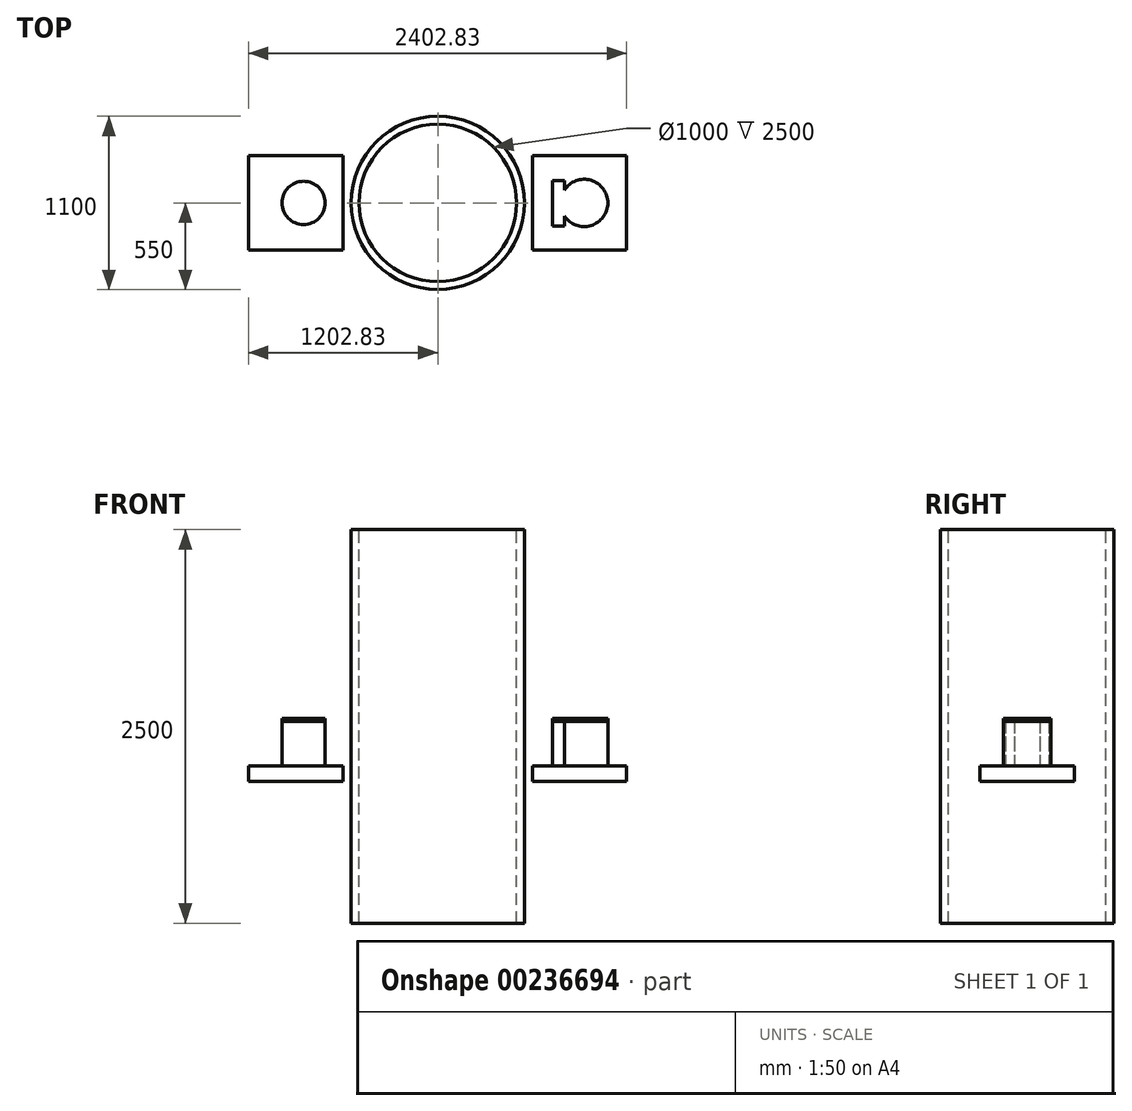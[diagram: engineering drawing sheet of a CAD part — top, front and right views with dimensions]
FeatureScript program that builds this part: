
annotation { "Feature Type Name" : "Feature", "Feature Type Description" : "" }
export const myFeature = defineFeature(function(context is Context, id is Id, definition is map)
    precondition{}
    {
        {
            var Q0;
            Q0=qCreatedBy(makeId("Top.planeOp"),FACE);
            var sketch = newSketch(context, id + "F0", { "sketchPlane" : qUnion([Q0])});
            skCircle(sketch, "E0", {"center": v(0, 0) * mm, "radius": 500 * mm});
            skCircle(sketch, "E1", {"center": v(0, 0) * mm, "radius": 550 * mm});
            skSolve(sketch);
        }
        {
            var Q0;
            Q0 = qSketchRegion(id + "F0", true);
            extrude(context, id + "F1", {"entities" : qUnion([Q0]), "oppositeDirection" : true, "depth" : 2500 * mm, "offsetDistance" : 25 * mm});
        }
        {
            var Q0;
            Q0=qCreatedBy(makeId("Front.planeOp"),FACE);
            var sketch = newSketch(context, id + "F2", { "sketchPlane" : qUnion([Q0])});
            skLineSegment(sketch, "E2.bottom", {"start": v(600, -1500) * mm, "end": v(1200, -1500) * mm});
            skLineSegment(sketch, "E2.top", {"start": v(600, -1600) * mm, "end": v(1200, -1600) * mm});
            skLineSegment(sketch, "E2.left", {"start": v(600, -1500) * mm, "end": v(600, -1600) * mm});
            skLineSegment(sketch, "E2.right", {"start": v(1200, -1500) * mm, "end": v(1200, -1600) * mm});
            skLineSegment(sketch, "E3.bottom", {"start": v(-602.83, -1500) * mm, "end": v(-1202.83, -1500) * mm});
            skLineSegment(sketch, "E3.top", {"start": v(-602.83, -1600) * mm, "end": v(-1202.83, -1600) * mm});
            skLineSegment(sketch, "E3.left", {"start": v(-602.83, -1500) * mm, "end": v(-602.83, -1600) * mm});
            skLineSegment(sketch, "E3.right", {"start": v(-1202.83, -1500) * mm, "end": v(-1202.83, -1600) * mm});
            skSolve(sketch);
        }
        {
            var Q0;
            Q0 = qSketchRegion(id + "F2", true);
            extrude(context, id + "F3", {"entities" : qUnion([Q0]), "depth" : 300 * mm, "offsetDistance" : 25 * mm, "hasSecondDirection" : true, "secondDirectionOppositeDirection" : true, "secondDirectionDepth" : 300 * mm});
        }
        {
            var Q0;
            Q0=makeQuery(id+"F3.opExtrude","SWEPT_FACE",FACE,{"disambiguationData":[OSD([sQuery(id+"F2.wireOp",EDGE,"E3.bottom")])]});
            var sketch = newSketch(context, id + "F4", { "sketchPlane" : qUnion([Q0])});
            skArc(sketch, "E4", {"start": v(804.42, -82.05) * mm, "mid": v(1080, 0) * mm, "end": v(804.42, 82.05) * mm});
            skLineSegment(sketch, "E5.bottom", {"start": v(728.65, 140.28) * mm, "end": v(804.42, 140.28) * mm});
            skLineSegment(sketch, "E5.top", {"start": v(728.65, -146.42) * mm, "end": v(804.42, -146.42) * mm});
            skLineSegment(sketch, "E5.left", {"start": v(728.65, 140.28) * mm, "end": v(728.65, -146.42) * mm});
            skLineSegment(sketch, "E5.right", {"start": v(804.42, 140.28) * mm, "end": v(804.42, 82.05) * mm});
            skLineSegment(sketch, "E6.trimOffspring", {"start": v(804.42, -82.05) * mm, "end": v(804.42, -146.42) * mm});
            skCircle(sketch, "E7", {"center": v(-852.3, 0) * mm, "radius": 137.3 * mm});
            skSolve(sketch);
        }
        {
            var Q0;
            Q0 = qSketchRegion(id + "F4", true);
            extrude(context, id + "F5", {"entities" : qUnion([Q0]), "operationType" : NewBodyOperationType.ADD, "depth" : 280 * mm, "offsetDistance" : 25 * mm});
        }
        {
            var Q0;
            Q0 = qSketchRegion(id + "F4", true);
            extrude(context, id + "F6", {"entities" : qUnion([Q0]), "depth" : 300 * mm, "offsetDistance" : 25 * mm});
        }
    });
